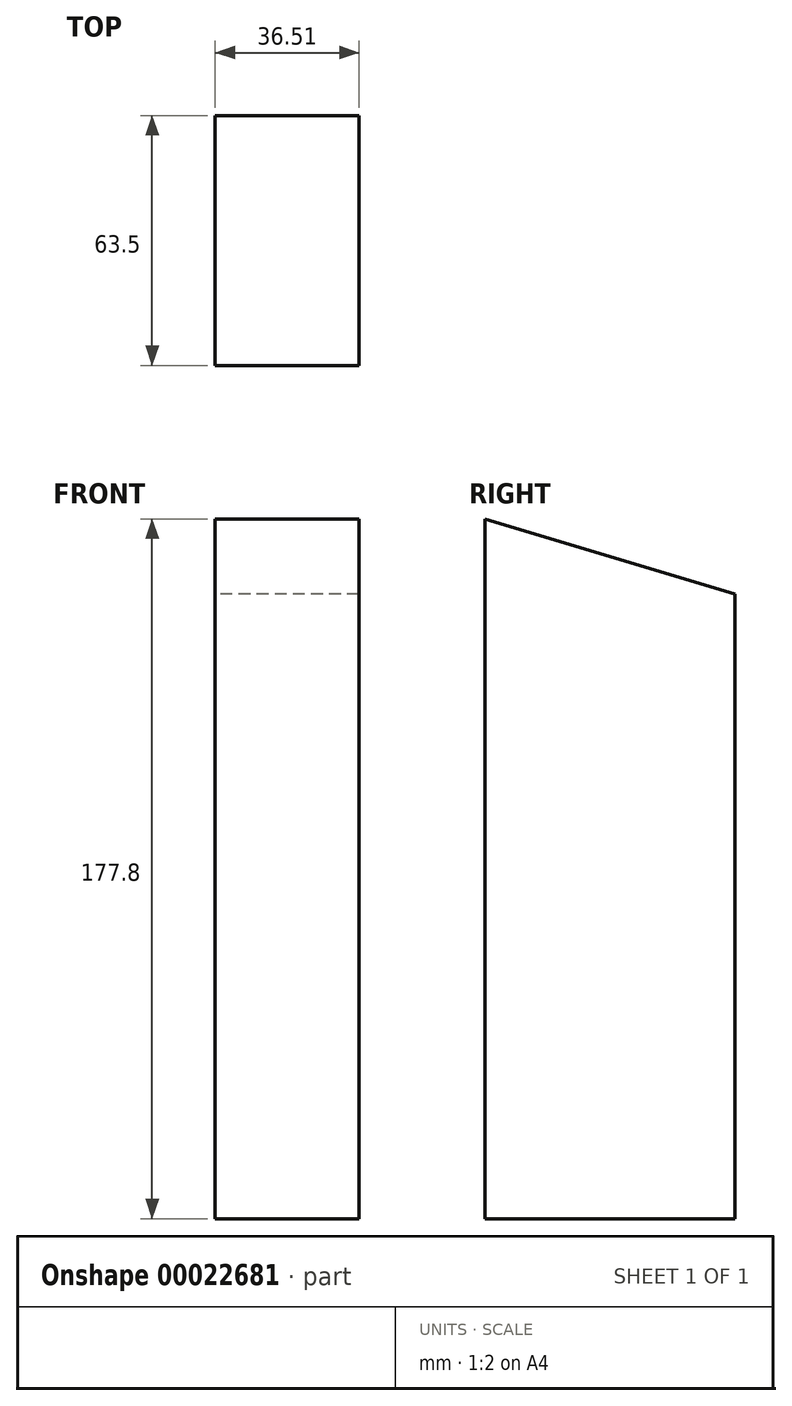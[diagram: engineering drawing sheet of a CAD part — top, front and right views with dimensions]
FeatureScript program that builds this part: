
annotation { "Feature Type Name" : "Feature", "Feature Type Description" : "" }
export const myFeature = defineFeature(function(context is Context, id is Id, definition is map)
    precondition{}
    {
        {
            var Q0;
            Q0=qCreatedBy(makeId("Right.planeOp"),FACE);
            var sketch = newSketch(context, id + "F0", { "sketchPlane" : qUnion([Q0])});
            skLineSegment(sketch, "E0", {"start": v(0, 0) * mm, "end": v(63.5, 0) * mm});
            skLineSegment(sketch, "E1", {"start": v(0, 0) * mm, "end": v(0, 177.8) * mm});
            skLineSegment(sketch, "E2", {"start": v(63.5, 0) * mm, "end": v(63.5, 158.75) * mm});
            skLineSegment(sketch, "E3", {"start": v(63.5, 158.75) * mm, "end": v(0, 177.8) * mm});
            skSolve(sketch);
        }
        {
            var Q0;
            Q0=qSketchRegion(id+"F0",true);
            extrude(context, id + "F1", {"entities" : qUnion([Q0]), "depth" : 36.5 * mm});
        }
    });
